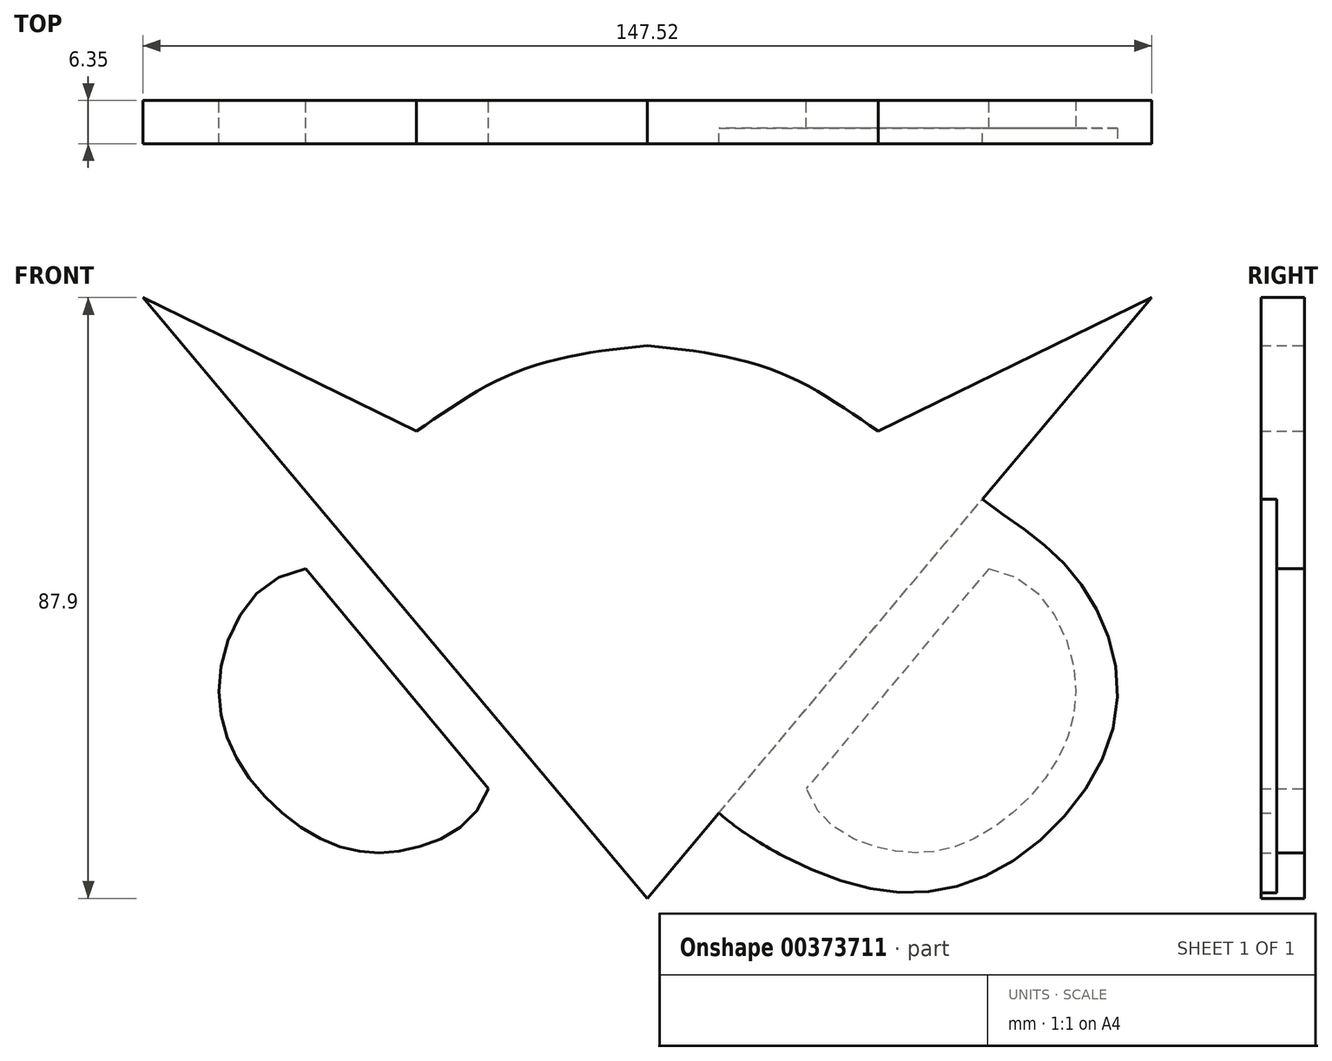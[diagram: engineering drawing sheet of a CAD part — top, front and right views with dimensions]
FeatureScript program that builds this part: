
annotation { "Feature Type Name" : "Feature", "Feature Type Description" : "" }
export const myFeature = defineFeature(function(context is Context, id is Id, definition is map)
    precondition{}
    {
        {
            var Q0;
            Q0=qCreatedBy(makeId("Front.planeOp"),FACE);
            var sketch = newSketch(context, id + "F0", { "sketchPlane" : qUnion([Q0])});
            skLineSegment(sketch, "E0", {"start": v(0, 30) * mm, "end": v(0, -50.87) * mm});
            skLineSegment(sketch, "E1", {"start": v(0, -50.87) * mm, "end": v(73.76, 37.03) * mm});
            skFitSpline(sketch, "E2", {"points": [v(49, 7.53) * mm, v(62.69, -3.86) * mm, v(68.27, -25.47) * mm, v(50.55, -47.08) * mm, v(28.82, -48.47) * mm, v(10.48, -38.38) * mm], "startDerivative": vector(77.25, -58.6) * mm, "endDerivative": vector(-54.57, 49.55) * mm});
            skFitSpline(sketch, "E3", {"points": [v(49.95, -2.6) * mm, v(62.46, -17.65) * mm, v(58.5, -32.92) * mm, v(46.35, -42.82) * mm, v(34.75, -43.66) * mm, v(23.24, -34.81) * mm], "startDerivative": vector(100.35, -14.58) * mm, "endDerivative": vector(-29.06, 85.06) * mm});
            skLineSegment(sketch, "E4", {"start": v(49.95, -2.6) * mm, "end": v(23.24, -34.81) * mm});
            skLineSegment(sketch, "E5", {"start": v(73.76, 37.03) * mm, "end": v(73.76, 37.03) * mm});
            skLineSegment(sketch, "E6", {"start": v(19.87, -44.67) * mm, "end": v(0, -68.35) * mm});
            skFitSpline(sketch, "E7", {"points": [v(33.76, 17.51) * mm, v(19.23, 26.12) * mm, v(0, 30) * mm], "startDerivative": vector(-28.1, 19.09) * mm, "endDerivative": vector(-38.63, 3.73) * mm});
            skLineSegment(sketch, "E8", {"start": v(73.76, 37.03) * mm, "end": v(33.76, 17.51) * mm});
            skPoint(sketch, "E9.orphan", {"position": v(0, 37.03) * mm});
            skLineSegment(sketch, "E10.MirrorCS", {"start": v(-73.76, 37.03) * mm, "end": v(-73.76, 37.03) * mm});
            skFitSpline(sketch, "E11.MirrorCS", {"points": [v(-33.76, 17.51) * mm, v(-19.23, 26.12) * mm, v(0, 30) * mm], "startDerivative": vector(28.1, 19.09) * mm, "endDerivative": vector(38.63, 3.73) * mm});
            skFitSpline(sketch, "E12.MirrorCS", {"points": [v(-49, 7.53) * mm, v(-62.69, -3.86) * mm, v(-68.27, -25.47) * mm, v(-50.55, -47.08) * mm, v(-28.82, -48.47) * mm, v(-10.48, -38.38) * mm], "startDerivative": vector(-77.25, -58.6) * mm, "endDerivative": vector(54.57, 49.55) * mm});
            skLineSegment(sketch, "E13.MirrorCS", {"start": v(-73.76, 37.03) * mm, "end": v(-33.76, 17.51) * mm});
            skFitSpline(sketch, "E14.MirrorCS", {"points": [v(-49.95, -2.6) * mm, v(-62.46, -17.65) * mm, v(-58.5, -32.92) * mm, v(-46.35, -42.82) * mm, v(-34.75, -43.66) * mm, v(-23.24, -34.81) * mm], "startDerivative": vector(-100.35, -14.58) * mm, "endDerivative": vector(29.06, 85.06) * mm});
            skLineSegment(sketch, "E15.MirrorCS", {"start": v(0, -50.87) * mm, "end": v(-73.76, 37.03) * mm});
            skLineSegment(sketch, "E16.MirrorCS", {"start": v(-19.87, -44.67) * mm, "end": v(0, -68.35) * mm});
            skLineSegment(sketch, "E17.MirrorCS", {"start": v(-49.95, -2.6) * mm, "end": v(-23.24, -34.81) * mm});
            skPoint(sketch, "E18.0.internal.snap0", {"position": v(-9.94, -56.51) * mm});
            skPoint(sketch, "E18.0.internal.orphan", {"position": v(0, -56.51) * mm});
            skSolve(sketch);
        }
        {
            var Q0;
            {var subQ1=sQuery(id+"F0.wireOp",EDGE,"E0");Q0=makeQuery(id+"F0.imprint","IMPRINT",FACE,{"disambiguationData":[TD([[makeQuery(id+"F0.imprint","IMPRINT",EDGE,{"derivedFrom":subQ1}),-1.0]])]});}
            var Q1;
            {var subQ3=sQuery(id+"F0.wireOp",EDGE,"E0");Q1=makeQuery(id+"F0.imprint","IMPRINT",FACE,{"disambiguationData":[TD([[makeQuery(id+"F0.imprint","IMPRINT",EDGE,{"derivedFrom":subQ3}),1.0]])]});}
            var Q2;
            {var subQ0=sQuery(id+"F0.wireOp",EDGE,"E2");Q2=makeQuery(id+"F0.imprint","IMPRINT",FACE,{"disambiguationData":[TD([[makeQuery(id+"F0.imprint","IMPRINT",EDGE,{"derivedFrom":subQ0}),-1.0]])]});}
            var Q3;
            Q3=makeQuery(id+"F0.imprint","IMPRINT",FACE,{"disambiguationData":[TD([[makeQuery(id+"F0.imprint","IMPRINT",EDGE,{"derivedFrom":sQuery(id+"F0.wireOp",EDGE,"E14.MirrorCS")}),1.0]])]});
            var Q4;
            Q4=makeQuery(id+"F0.imprint","IMPRINT",FACE,{"disambiguationData":[TD([[makeQuery(id+"F0.imprint","IMPRINT",EDGE,{"derivedFrom":sQuery(id+"F0.wireOp",EDGE,"E3")}),-1.0]])]});
            extrude(context, id + "F1", {"entities" : qUnion([Q0, Q1, Q2, Q3, Q4]), "depth" : 6.35 * mm});
        }
        {
            var Q0;
            {var subQ0=sQuery(id+"F0.wireOp",EDGE,"E2");Q0=makeQuery(id+"F0.imprint","IMPRINT",FACE,{"disambiguationData":[TD([[makeQuery(id+"F0.imprint","IMPRINT",EDGE,{"derivedFrom":subQ0}),-1.0]])]});}
            extrude(context, id + "F2", {"entities" : qUnion([Q0]), "operationType" : NewBodyOperationType.REMOVE, "depth" : 4.06 * mm});
        }
    });
